# Revit family: Haworth_BuzziBalance_Board
name_source: partatom
category: Furniture
revit_build: Autodesk Revit 2018 (Build: 20170223_1515(x64)
units: mm (PartAtom-declared; Revit-internal decimal feet)

## family parameters
Always vertical = Yes
Cut with Voids When Loaded = No
OmniClass Number = 23.40.70.14.64.21
OmniClass Title = Systems Furniture
Room Calculation Point = No
Shared = No
Work Plane-Based = No

## types (2) — shared parameters
Actual Height = 2.76 "
Assembly Code = E2020200
Manufacturer = Haworth
Model = HCBZ-BAAB
Revision Number = 1
Size = Verify Final Dim. w/ Haworth
URL = http://www.haworth.com
URL - Product = https://www.haworth.com
Warranty = http://www.haworth.com
Wood Finish = Haworth _ Wood _ Collection _ Ash Natural

## per-type parameters (varying)
| type | Actual Depth | Actual Width | Description | Large | Radius | Small |
| HCBZ-BAAB - Small | 21.65 " | 21.65 " | Haworth BuzziBalance - Small Board | No | 10.82 " | Yes |
| HCBZ-BAAB - Large | 38.19 " | 38.19 " | Haworth BuzziBalance Large Board | Yes | 19.1 " | No |

## geometry (parser evidence)
native form markers: Sweep x3
no freeform markers — native parametric forms only
